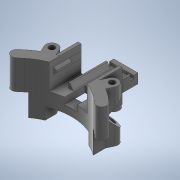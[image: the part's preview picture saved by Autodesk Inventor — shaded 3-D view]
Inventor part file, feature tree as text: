
AUTODESK INVENTOR PART (.ipt)
format: ipt  version: 2020 (Build 240168000, 168)  size: 730,624 bytes
history: native  units: mm
features: extrude x17, sketch x16, projected_geometry x14, other x5, sweep x1, chamfer x1
ambient origin geometry x8: Origin, YZ Plane, XZ Plane, XY Plane, X Axis, Y Axis, Z Axis, Center Point
bodies: Body1 (feature_tree)
feature tree (54):
  other  "Твердое тело1"
  extrude  "Выдавливание1"  Depth=35.0mm TaperAngle=0.0deg
  sketch  "Эскиз2"
  extrude  "Выдавливание2"  Depth=4.0mm
  sweep  "Сдвиг1"
  extrude  "Выдавливание5"  Depth=8.0mm
  extrude  "Выдавливание6"  Depth=35.0mm TaperAngle=0.0deg
  extrude  "Выдавливание7"  Depth=8.5mm
  extrude  "Выдавливание8"  TaperAngle=45.0deg  [1 undecoded]
  other  "РабПлоскость1"
  extrude  "Выдавливание9"  Depth=8.5mm
  extrude  "Выдавливание10"  TaperAngle=45.0deg  [1 undecoded]
  extrude  "Выдавливание11"  TaperAngle=0.0deg  [1 undecoded]
  sketch  "Эскиз13"
  other  "РабПлоскость2"
  sketch  "Эскиз14"
  extrude  "Выдавливание12"  Depth=5.0mm TaperAngle=0.0deg
  extrude  "Выдавливание13"  Depth=15.0mm TaperAngle=0.0deg
  other  "РабПлоскость3"
  extrude  "Выдавливание14"  Depth=15.0mm TaperAngle=0.0deg
  extrude  "Выдавливание15"  Depth=26.0mm
  extrude  "Выдавливание16"  Depth=6.0mm
  extrude  "Выдавливание17"  Depth=15.0mm TaperAngle=0.0deg
  chamfer  "Фаска1"  Distance=2.0mm
  other  "РабПлоскость4"
  sketch  "Эскиз18"
  extrude  "Выдавливание18"  Depth=1.5mm
  extrude  "Выдавливание19"  Depth=3.0mm
  sketch  "Эскиз1"
  sketch  "Эскиз3"
  projected_geometry  "Спроецированная петля1"
  projected_geometry  "Спроецированная петля2"
  sketch  "3D эскиз1"
  sketch  "Эскиз4"
  sketch  "Эскиз6"
  projected_geometry  "Спроецированная петля4"
  sketch  "Эскиз7"
  projected_geometry  "Спроецированная петля5"
  sketch  "Эскиз9"
  projected_geometry  "Спроецированная петля7"
  sketch  "Эскиз11"
  projected_geometry  "Спроецированная петля8"
  sketch  "Эскиз12"
  projected_geometry  "Спроецированная петля9"
  projected_geometry  "Спроецированная петля10"
  sketch  "Эскиз15"
  sketch  "Эскиз16"
  projected_geometry  "Спроецированная петля11"
  projected_geometry  "Спроецированная петля12"
  sketch  "Эскиз17"
  projected_geometry  "Спроецированная петля13"
  projected_geometry  "Спроецированная петля14"
  projected_geometry  "Спроецированная петля15"
  projected_geometry  "Спроецированная петля16"
note: 3 required parameter values undecoded (feature->parameter linkage not recoverable at this tier; creation-order binding heuristic only, values carry confidence <= 0.55)
